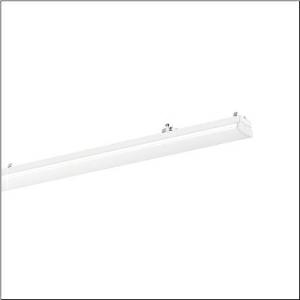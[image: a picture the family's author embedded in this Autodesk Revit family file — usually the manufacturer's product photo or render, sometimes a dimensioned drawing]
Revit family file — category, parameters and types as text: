
# Revit family: licross_21_recessed_opal_mo_52te1ddn46xg
name_source: partatom
category: Lighting Fixtures
units: mm (PartAtom-declared; Revit-internal decimal feet)

## family parameters
Cut with Voids When Loaded = No
Host = Face
Light Source = No
Part Type = Normal
Room Calculation Point = No
Round Connector Dimension = Use Diameter
Shared = No

## types (1)
- --- (1 x LED, 6320 lm, 36.1 W, 4000K)
    Apparent Load = 36 VA
    CIE Flux Codes = 44 73 91 87 100
    Color Rendering = 80
    Color Temperature = 4000K
    Default Elevation = 1800 mm
    Description = Licross 21 recessed opal MO, luminaire insert, of sheet steel, galvanised, coil coated, white, length: 1.500mm, width: 66mm, height: 67mm, LED rated luminous flux: 6.320lm, light colour: 840, SDCM (Standard Deviation of Colour Matching)MacAdam ≤ 3 SDCM (initial), control gear: DALI 2, with plug, 5-pole, with phase selection, mains connection: 220..240V, AC, 50/60Hz, rated input power: 36W, internal wiring halogen-free, primary optical cover: cover, of PMMA, light emission: direct with ceiling illumination distribution, primary light characteristic: symmetric, protection rating (complete): IP54, insulation class (complete): insulation class I (protective earthing), certification: CE, ENEC, VDE, UKCA, protection symbol: D if used in an environment with non-conductive dust loads with corresponding accessories, impact resistance: IK06, permissible ambient temperature for indoor applications: -25..+40°C, corresponds to IFS (International Featured Standards) requirements for safety and quality in the food industry, reducing of maximum allowable ambient temperature of 5°C with ceiling mounting, LABS conformity tested according to VDMA 24364:2018-05, The light source and the operating device comply with the requirements of the Ecodesign Regulation (EU) 2019/2020 and are replaceable in accordance with this regulation, packaging unit: 1 piece
    Height = 83 mm
    Lamp = 1 x LED
    Lamp Light Flux = 6320 lm
    Lamp Power = 36.1 W
    Lamp count = 1
    Length = 1500 mm
    Luminous efficacy = 175 lm/W
    Manufacturer = Siteco
    ModVariant = No
    Model = 52TE1DDN46XG
    Mounting Place = Ceiling
    Mounting Type = Pendant
    Number of Poles = 1
    OnlyDefault = Yes
    Power Factor = 1
    Product Name = Licross 21 recessed opal MO
    Product group = luminaire insert | ceiling pendant
    ProductGroupID = 901
    Protection Class = Protection class I
    Protection Degree = IP 54
    RLX_Detail_Level = 1
    RLX_Emergency_Light_Flux = 0 lm
    RLX_Emergency_Type = 0
    RLX_Emergency_Type_DB = No
    RlxData = <blob elided: 26749 chars, md5=43349875>
    Socket = socket
    Standby Power = 0 W
    System Light Flux = 6320 lm
    System Power = 36 W
    Type Comments = factory setting: luminous flux: 100 % | dim-lin: 254 | 245 mA
    Type Image = l_1313666.jpg
    URL = http://relux.com
    VarID = @adj_076127
    Voltage = 0 V
    Weight = 0.00 kg
    Width = 76 mm

## geometry (parser evidence)
native form markers: Blend x4, Sweep x13
no freeform markers — native parametric forms only
